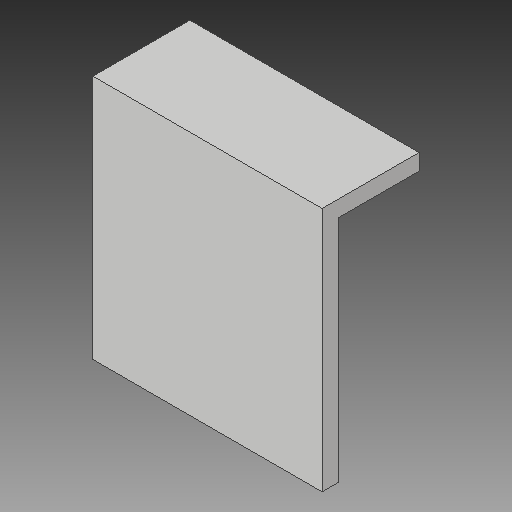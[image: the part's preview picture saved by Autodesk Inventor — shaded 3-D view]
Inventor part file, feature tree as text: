
AUTODESK INVENTOR PART (.ipt)
format: ipt  version: 2017 (Build 210142000, 142)  size: 100,864 bytes
history: native  units: in
note: dims shown in document units (in); Inventor stores cm internally (conversion verified against a paired STEP export)
features: extrude x3, sketch x3
ambient origin geometry x8: Origin, YZ Plane, XZ Plane, XY Plane, X Axis, Y Axis, Z Axis, Center Point
bodies: Solid1 (feature_tree)
feature tree (6):
  extrude  "Extrusion1"  Depth=0.709in
  extrude  "Extrusion2"  Depth=0.05in
  extrude  "Extrusion3"  Depth=0.05in TaperAngle=0.0deg
  sketch  "Sketch1"  dims[d0=0.709in d1=0.709in]
  sketch  "Sketch2"  dims[d2=0.05in d3=0.0in d4=0.25in]
  sketch  "Sketch3"  dims[d5=0.05in d6=0.0in d7=0.05in d8=0.0in]
